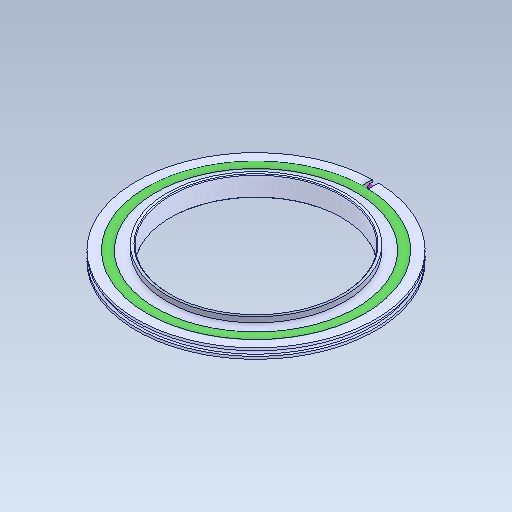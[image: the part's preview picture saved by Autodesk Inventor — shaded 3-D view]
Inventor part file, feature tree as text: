
AUTODESK INVENTOR PART (.ipt)
format: ipt  version: 2021 (Build 250183000, 183)  size: 258,560 bytes
history: native  units: in
note: dims shown in document units (in); Inventor stores cm internally (conversion verified against a paired STEP export)
features: revolve x2, chamfer x1, other x1
ambient origin geometry x8: Origin, YZ Plane, XZ Plane, XY Plane, X Axis, Y Axis, Z Axis, Center Point
bodies: Solid1 (feature_tree), Solid2 (feature_tree), Solid3 (feature_tree), Solid4 (feature_tree)
feature tree (4):
  chamfer  "Chamfer1"  [1 undecoded]
  revolve  "Revolve2"  [1 undecoded]
  other  "Cut-Extrude1"
  revolve  "Revolve4"  [1 undecoded]
note: 3 required parameter values undecoded (feature->parameter linkage not recoverable at this tier; creation-order binding heuristic only, values carry confidence <= 0.55)
